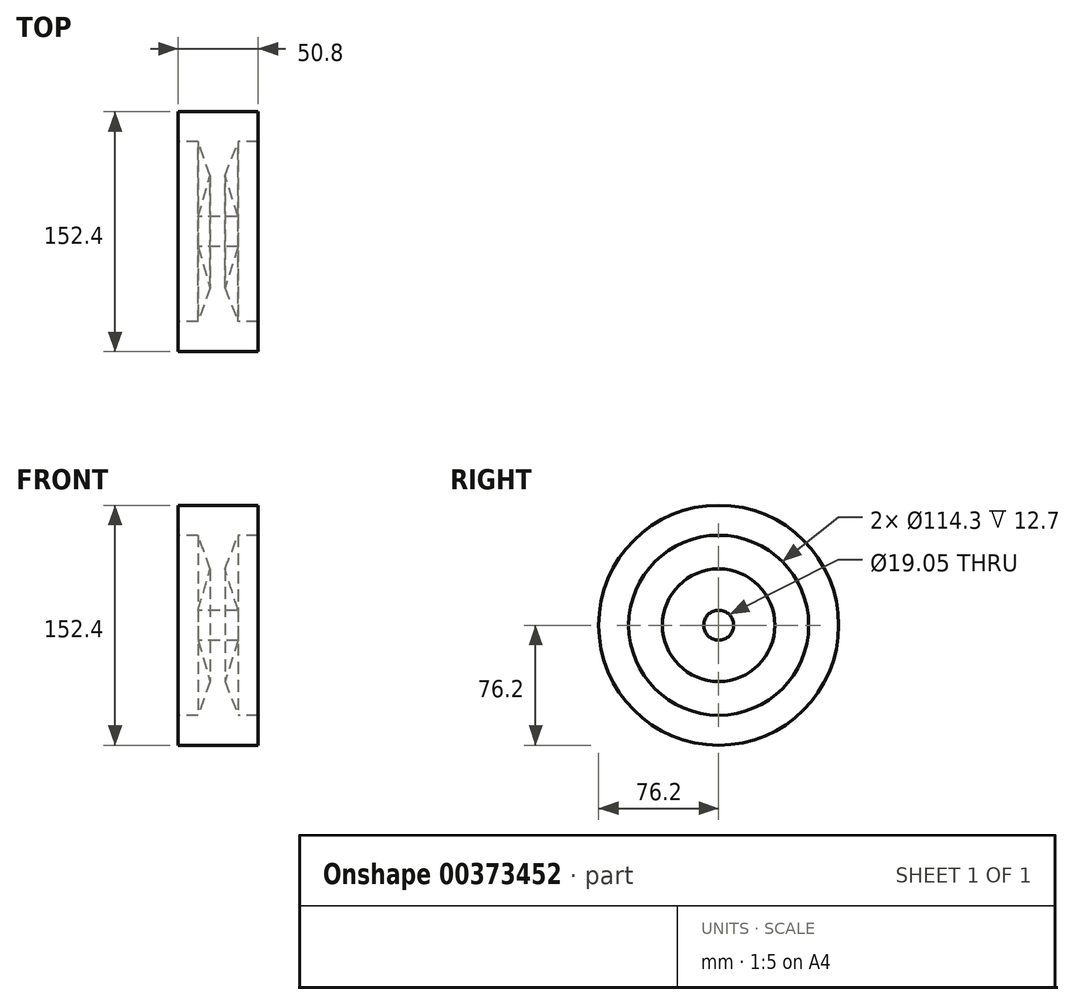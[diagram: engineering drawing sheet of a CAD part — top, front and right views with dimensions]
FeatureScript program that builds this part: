
annotation { "Feature Type Name" : "Feature", "Feature Type Description" : "" }
export const myFeature = defineFeature(function(context is Context, id is Id, definition is map)
    precondition{}
    {
        {
            var Q0;
            Q0=qCreatedBy(makeId("Front.planeOp"),FACE);
            var sketch = newSketch(context, id + "F0", { "sketchPlane" : qUnion([Q0])});
            skLineSegment(sketch, "E0", {"start": v(-22.38, 0) * mm, "end": v(34.33, 0) * mm});
            skLineSegment(sketch, "E1", {"start": v(-12.7, 9.52) * mm, "end": v(12.7, 9.53) * mm});
            skLineSegment(sketch, "E2", {"start": v(12.7, 9.53) * mm, "end": v(4.35, 35.76) * mm});
            skLineSegment(sketch, "E3", {"start": v(4.35, 35.76) * mm, "end": v(12.7, 57.15) * mm});
            skLineSegment(sketch, "E4", {"start": v(12.7, 57.15) * mm, "end": v(25.4, 57.15) * mm});
            skLineSegment(sketch, "E5", {"start": v(25.4, 57.15) * mm, "end": v(25.4, 76.2) * mm});
            skLineSegment(sketch, "E6", {"start": v(25.4, 76.2) * mm, "end": v(-25.4, 76.2) * mm});
            skLineSegment(sketch, "E7", {"start": v(-25.4, 76.2) * mm, "end": v(-25.4, 57.15) * mm});
            skLineSegment(sketch, "E8", {"start": v(-25.4, 57.15) * mm, "end": v(-12.7, 57.15) * mm});
            skLineSegment(sketch, "E9", {"start": v(-12.7, 57.15) * mm, "end": v(-5.14, 35.76) * mm});
            skLineSegment(sketch, "E10", {"start": v(-5.14, 35.76) * mm, "end": v(-12.7, 9.52) * mm});
            skSolve(sketch);
        }
        {
            var Q0;
            Q0=makeQuery(id+"F0.imprint","IMPRINT",FACE,{"disambiguationData":[TD([[makeQuery(id+"F0.imprint","IMPRINT",EDGE,{"derivedFrom":sQuery(id+"F0.wireOp",EDGE,"E1")}),1.0]])]});
            var Q1;
            Q1=sQuery(id+"F0.wireOp",EDGE,"E0");
            revolve(context, id + "F1", {"entities" : qUnion([Q0]), "axis" : qUnion([Q1]), "revolveType" : RevolveType.FULL});
        }
    });
